# Revit family: Bath-Freestanding-KOHLER-Volute-K-23074T_1
name_source: partatom
category: Plumbing Fixtures
units: mm (PartAtom-declared; Revit-internal decimal feet)

## family parameters
Cut with Voids When Loaded = No
Host = Face
Maintain Annotation Orientation = No
OmniClass Number = 23.31.15.00
Part Type = Normal
Room Calculation Point = No
Round Connector Dimension = Use Diameter
Shared = No

## types (4) — shared parameters
ADA Compliant = No
Assembly Code = D2010500
CW Connection = No
Cold Water Inlet = Cold Water Inlet
Date Modified = 01/21/2025
Default Elevation = 0"
Drain Included = No
HW Connection = No
Height = 21 1/16"
Hot Water Inlet = Hot Water Inlet
Length = 66 15/16"
Manufacturer = Kohler Co.
Master Format 2014 = 22 41 19
Master Format 2014 Name = Residential Bathtubs
Material = Cast Iron
Product Documentation Link = https://files.kohler.com.cn
Product Name = Volute
Product Page URL = https://www.kohler.com.cn
URL = http://www.kohler.com.cn
Vent Connection = No
Waste Connection = Yes
Waste Water Outlet = Waste Water Outlet
WaterSense Certified = No
Width = 31 1/2"

## per-type parameters (varying)
| type | Description | Finish | Grab Bar | Model | No Grab Bar | Secondary Finish | Type |
| With Grab Bar, 0-White | 1.7m freestanding cast iron bathtub (rose gold skirt with armrests) | KOHLER-Cast_Iron-0-White | Yes | K-23074T-GR-0 | No | KOHLER-Cast_Iron-0-White | 1 |
| With Grab Bar, 7-Black Black | 1.7m freestanding cast iron bathtub (rose gold skirt, basalt black, with armrests) | KOHLER-Cast_Iron-7-Black_Black | Yes | K-23074T-GR-7 | No | KOHLER-Cast_Iron-P5-Iron_Black | 2 |
| Without Grab Bar, 0-White | 1.7m freestanding cast iron bathtub with rose gold skirt | KOHLER-Cast_Iron-0-White | No | K-23074T-0 | Yes | KOHLER-Cast_Iron-0-White | 3 |
| Without Grab Bar, 7-Black Black | 1.7m freestanding cast iron bathtub (rose gold skirt, basalt black) | KOHLER-Cast_Iron-7-Black_Black | No | K-23074T-7 | Yes | KOHLER-Cast_Iron-P5-Iron_Black | 4 |

## geometry (parser evidence)
native form markers: Sweep x8
no freeform markers — native parametric forms only
